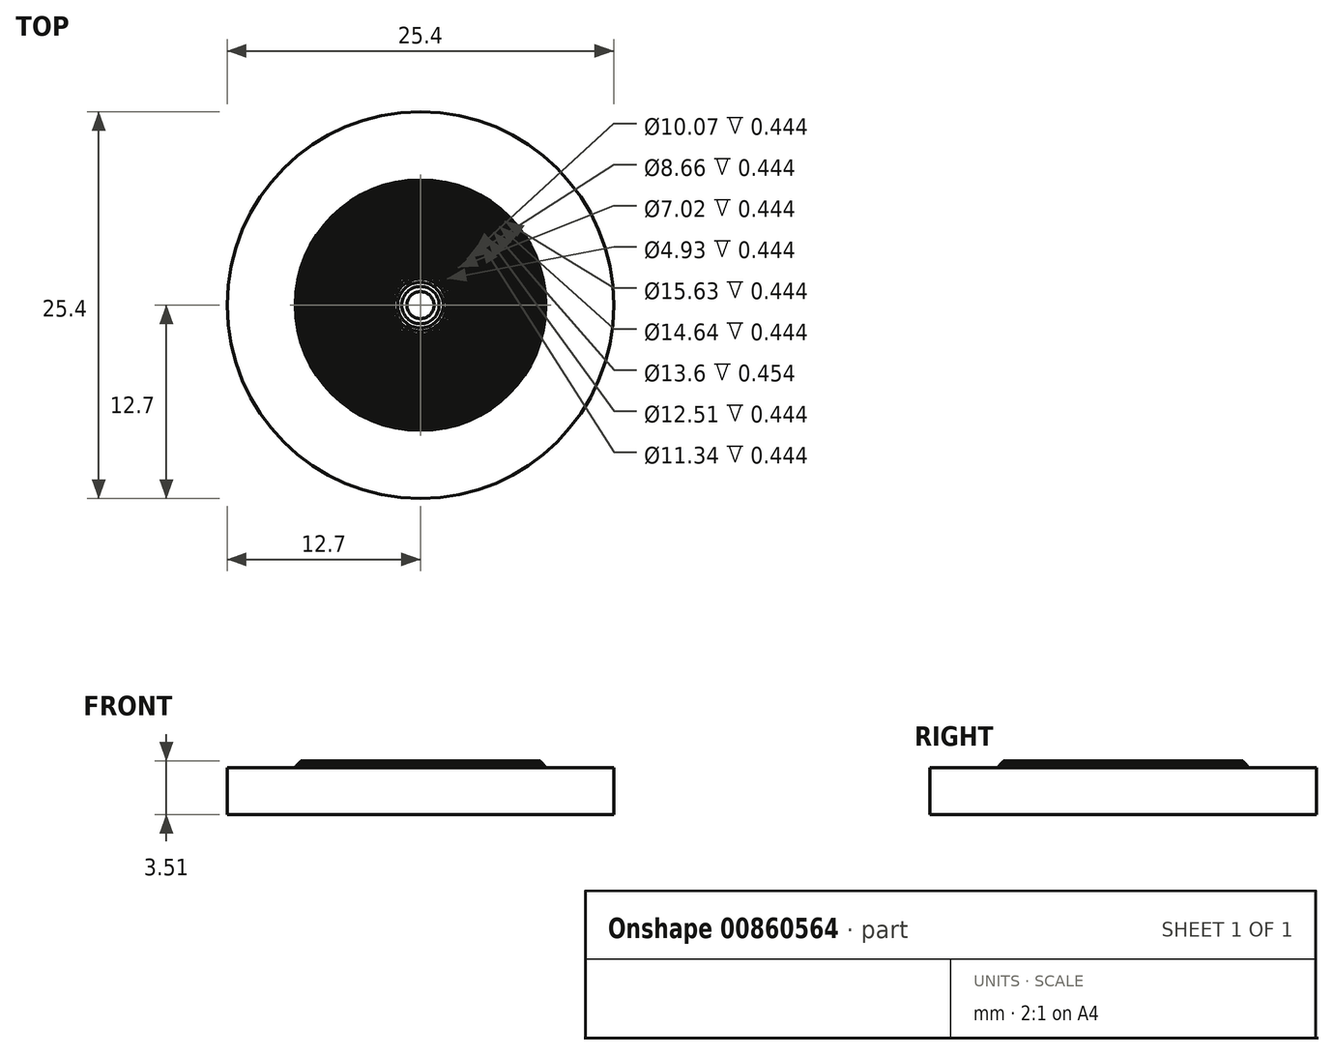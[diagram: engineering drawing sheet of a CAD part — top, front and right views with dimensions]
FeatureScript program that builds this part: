
annotation { "Feature Type Name" : "Feature", "Feature Type Description" : "" }
export const myFeature = defineFeature(function(context is Context, id is Id, definition is map)
    precondition{}
    {
        {
            var Q0;
            Q0=qCreatedBy(makeId("Front.planeOp"),FACE);
            var sketch = newSketch(context, id + "F0", { "sketchPlane" : qUnion([Q0])});
            skLineSegment(sketch, "E0", {"start": v(0, 0) * mm, "end": v(0, 3.5) * mm});
            skLineSegment(sketch, "E1", {"start": v(0, 3.5) * mm, "end": v(0.89, 3.5) * mm});
            skLineSegment(sketch, "E2", {"start": v(0.89, 3.5) * mm, "end": v(0.89, 3.44) * mm});
            skLineSegment(sketch, "E3", {"start": v(1.23, 3.38) * mm, "end": v(1.23, 3.44) * mm});
            skLineSegment(sketch, "E4", {"start": v(1.23, 3.44) * mm, "end": v(0.89, 3.44) * mm});
            skLineSegment(sketch, "E5", {"start": v(1.5, 3.32) * mm, "end": v(1.5, 3.38) * mm});
            skLineSegment(sketch, "E6", {"start": v(1.5, 3.38) * mm, "end": v(1.23, 3.38) * mm});
            skLineSegment(sketch, "E7", {"start": v(1.74, 3.25) * mm, "end": v(1.74, 3.32) * mm});
            skLineSegment(sketch, "E8", {"start": v(1.74, 3.32) * mm, "end": v(1.5, 3.32) * mm});
            skLineSegment(sketch, "E9", {"start": v(1.94, 3.19) * mm, "end": v(1.94, 3.25) * mm});
            skLineSegment(sketch, "E10", {"start": v(1.94, 3.25) * mm, "end": v(1.74, 3.25) * mm});
            skLineSegment(sketch, "E11", {"start": v(2.13, 3.13) * mm, "end": v(2.13, 3.19) * mm});
            skLineSegment(sketch, "E12", {"start": v(2.13, 3.19) * mm, "end": v(1.94, 3.19) * mm});
            skLineSegment(sketch, "E13", {"start": v(2.3, 3.06) * mm, "end": v(2.3, 3.13) * mm});
            skLineSegment(sketch, "E14", {"start": v(2.3, 3.13) * mm, "end": v(2.13, 3.13) * mm});
            skLineSegment(sketch, "E15", {"start": v(2.46, 3.06) * mm, "end": v(2.3, 3.06) * mm});
            skLineSegment(sketch, "E16", {"start": v(2.9, 3.32) * mm, "end": v(2.9, 3.38) * mm});
            skLineSegment(sketch, "E17", {"start": v(2.9, 3.38) * mm, "end": v(2.76, 3.38) * mm});
            skLineSegment(sketch, "E18", {"start": v(3.03, 3.25) * mm, "end": v(3.03, 3.32) * mm});
            skLineSegment(sketch, "E19", {"start": v(3.03, 3.32) * mm, "end": v(2.9, 3.32) * mm});
            skLineSegment(sketch, "E20", {"start": v(3.16, 3.19) * mm, "end": v(3.16, 3.25) * mm});
            skLineSegment(sketch, "E21", {"start": v(3.16, 3.25) * mm, "end": v(3.03, 3.25) * mm});
            skLineSegment(sketch, "E22", {"start": v(2.46, 3.06) * mm, "end": v(2.46, 3.5) * mm});
            skLineSegment(sketch, "E23", {"start": v(2.46, 3.5) * mm, "end": v(2.62, 3.5) * mm});
            skLineSegment(sketch, "E24", {"start": v(2.76, 3.38) * mm, "end": v(2.76, 3.44) * mm});
            skLineSegment(sketch, "E25", {"start": v(2.76, 3.44) * mm, "end": v(2.62, 3.44) * mm});
            skLineSegment(sketch, "E26", {"start": v(3.28, 3.13) * mm, "end": v(3.28, 3.19) * mm});
            skLineSegment(sketch, "E27", {"start": v(3.28, 3.19) * mm, "end": v(3.16, 3.19) * mm});
            skLineSegment(sketch, "E28", {"start": v(3.4, 3.06) * mm, "end": v(3.4, 3.13) * mm});
            skLineSegment(sketch, "E29", {"start": v(3.4, 3.13) * mm, "end": v(3.28, 3.13) * mm});
            skLineSegment(sketch, "E30", {"start": v(3.51, 3.06) * mm, "end": v(3.4, 3.06) * mm});
            skLineSegment(sketch, "E31", {"start": v(3.62, 3.44) * mm, "end": v(3.62, 3.5) * mm});
            skLineSegment(sketch, "E32", {"start": v(3.73, 3.38) * mm, "end": v(3.73, 3.44) * mm});
            skLineSegment(sketch, "E33", {"start": v(3.73, 3.44) * mm, "end": v(3.62, 3.44) * mm});
            skLineSegment(sketch, "E34", {"start": v(3.51, 3.5) * mm, "end": v(3.62, 3.5) * mm});
            skLineSegment(sketch, "E35", {"start": v(3.84, 3.32) * mm, "end": v(3.84, 3.38) * mm});
            skLineSegment(sketch, "E36", {"start": v(3.84, 3.38) * mm, "end": v(3.73, 3.38) * mm});
            skLineSegment(sketch, "E37", {"start": v(3.94, 3.25) * mm, "end": v(3.94, 3.32) * mm});
            skLineSegment(sketch, "E38", {"start": v(3.94, 3.32) * mm, "end": v(3.84, 3.32) * mm});
            skLineSegment(sketch, "E39", {"start": v(4.04, 3.19) * mm, "end": v(4.04, 3.25) * mm});
            skLineSegment(sketch, "E40", {"start": v(4.04, 3.25) * mm, "end": v(3.94, 3.25) * mm});
            skLineSegment(sketch, "E41", {"start": v(4.14, 3.13) * mm, "end": v(4.14, 3.19) * mm});
            skLineSegment(sketch, "E42", {"start": v(4.14, 3.19) * mm, "end": v(4.04, 3.19) * mm});
            skLineSegment(sketch, "E43", {"start": v(4.24, 3.06) * mm, "end": v(4.24, 3.13) * mm});
            skLineSegment(sketch, "E44", {"start": v(4.24, 3.13) * mm, "end": v(4.14, 3.13) * mm});
            skLineSegment(sketch, "E45", {"start": v(4.33, 3.06) * mm, "end": v(4.24, 3.06) * mm});
            skLineSegment(sketch, "E46", {"start": v(4.42, 3.44) * mm, "end": v(4.42, 3.5) * mm});
            skLineSegment(sketch, "E47", {"start": v(4.33, 3.06) * mm, "end": v(4.33, 3.5) * mm});
            skLineSegment(sketch, "E48", {"start": v(4.33, 3.5) * mm, "end": v(4.42, 3.5) * mm});
            skLineSegment(sketch, "E49", {"start": v(4.51, 3.38) * mm, "end": v(4.51, 3.44) * mm});
            skLineSegment(sketch, "E50", {"start": v(4.51, 3.44) * mm, "end": v(4.42, 3.44) * mm});
            skLineSegment(sketch, "E51", {"start": v(4.6, 3.32) * mm, "end": v(4.6, 3.38) * mm});
            skLineSegment(sketch, "E52", {"start": v(4.6, 3.38) * mm, "end": v(4.51, 3.38) * mm});
            skLineSegment(sketch, "E53", {"start": v(4.7, 3.25) * mm, "end": v(4.7, 3.32) * mm});
            skLineSegment(sketch, "E54", {"start": v(4.7, 3.32) * mm, "end": v(4.6, 3.32) * mm});
            skLineSegment(sketch, "E55", {"start": v(4.78, 3.19) * mm, "end": v(4.78, 3.25) * mm});
            skLineSegment(sketch, "E56", {"start": v(4.78, 3.25) * mm, "end": v(4.7, 3.25) * mm});
            skLineSegment(sketch, "E57", {"start": v(4.87, 3.13) * mm, "end": v(4.87, 3.19) * mm});
            skLineSegment(sketch, "E58", {"start": v(4.87, 3.19) * mm, "end": v(4.78, 3.19) * mm});
            skLineSegment(sketch, "E59", {"start": v(4.95, 3.06) * mm, "end": v(4.95, 3.13) * mm});
            skLineSegment(sketch, "E60", {"start": v(4.95, 3.13) * mm, "end": v(4.87, 3.13) * mm});
            skLineSegment(sketch, "E61", {"start": v(5.04, 3.06) * mm, "end": v(4.95, 3.06) * mm});
            skLineSegment(sketch, "E62", {"start": v(5.12, 3.44) * mm, "end": v(5.12, 3.5) * mm});
            skLineSegment(sketch, "E63", {"start": v(5.04, 3.5) * mm, "end": v(5.12, 3.5) * mm});
            skLineSegment(sketch, "E64", {"start": v(5.2, 3.38) * mm, "end": v(5.2, 3.44) * mm});
            skLineSegment(sketch, "E65", {"start": v(5.2, 3.44) * mm, "end": v(5.12, 3.44) * mm});
            skLineSegment(sketch, "E66", {"start": v(5.28, 3.32) * mm, "end": v(5.28, 3.38) * mm});
            skLineSegment(sketch, "E67", {"start": v(5.28, 3.38) * mm, "end": v(5.2, 3.38) * mm});
            skLineSegment(sketch, "E68", {"start": v(5.36, 3.25) * mm, "end": v(5.36, 3.32) * mm});
            skLineSegment(sketch, "E69", {"start": v(5.36, 3.32) * mm, "end": v(5.28, 3.32) * mm});
            skLineSegment(sketch, "E70", {"start": v(5.44, 3.19) * mm, "end": v(5.44, 3.25) * mm});
            skLineSegment(sketch, "E71", {"start": v(5.44, 3.25) * mm, "end": v(5.36, 3.25) * mm});
            skLineSegment(sketch, "E72", {"start": v(5.52, 3.13) * mm, "end": v(5.52, 3.19) * mm});
            skLineSegment(sketch, "E73", {"start": v(5.52, 3.19) * mm, "end": v(5.44, 3.19) * mm});
            skLineSegment(sketch, "E74", {"start": v(5.6, 3.06) * mm, "end": v(5.6, 3.13) * mm});
            skLineSegment(sketch, "E75", {"start": v(5.6, 3.13) * mm, "end": v(5.52, 3.13) * mm});
            skLineSegment(sketch, "E76", {"start": v(5.67, 3.06) * mm, "end": v(5.6, 3.06) * mm});
            skLineSegment(sketch, "E77", {"start": v(5.74, 3.44) * mm, "end": v(5.74, 3.5) * mm});
            skLineSegment(sketch, "E78", {"start": v(5.67, 3.5) * mm, "end": v(5.74, 3.5) * mm});
            skLineSegment(sketch, "E79", {"start": v(5.82, 3.38) * mm, "end": v(5.82, 3.44) * mm});
            skLineSegment(sketch, "E80", {"start": v(5.82, 3.44) * mm, "end": v(5.74, 3.44) * mm});
            skLineSegment(sketch, "E81", {"start": v(5.9, 3.32) * mm, "end": v(5.9, 3.38) * mm});
            skLineSegment(sketch, "E82", {"start": v(5.9, 3.38) * mm, "end": v(5.82, 3.38) * mm});
            skLineSegment(sketch, "E83", {"start": v(5.97, 3.25) * mm, "end": v(5.97, 3.32) * mm});
            skLineSegment(sketch, "E84", {"start": v(5.97, 3.32) * mm, "end": v(5.9, 3.32) * mm});
            skLineSegment(sketch, "E85", {"start": v(6.04, 3.19) * mm, "end": v(6.04, 3.25) * mm});
            skLineSegment(sketch, "E86", {"start": v(6.04, 3.25) * mm, "end": v(5.97, 3.25) * mm});
            skLineSegment(sketch, "E87", {"start": v(6.18, 3.06) * mm, "end": v(6.18, 3.13) * mm});
            skLineSegment(sketch, "E88", {"start": v(6.11, 3.13) * mm, "end": v(6.11, 3.19) * mm});
            skLineSegment(sketch, "E89", {"start": v(6.11, 3.19) * mm, "end": v(6.04, 3.19) * mm});
            skLineSegment(sketch, "E90", {"start": v(6.18, 3.13) * mm, "end": v(6.11, 3.13) * mm});
            skLineSegment(sketch, "E91", {"start": v(6.25, 3.06) * mm, "end": v(6.18, 3.06) * mm});
            skLineSegment(sketch, "E92", {"start": v(6.32, 3.44) * mm, "end": v(6.32, 3.5) * mm});
            skLineSegment(sketch, "E93", {"start": v(6.25, 3.06) * mm, "end": v(6.25, 3.5) * mm});
            skLineSegment(sketch, "E94", {"start": v(6.25, 3.5) * mm, "end": v(6.32, 3.5) * mm});
            skLineSegment(sketch, "E95", {"start": v(6.4, 3.38) * mm, "end": v(6.4, 3.44) * mm});
            skLineSegment(sketch, "E96", {"start": v(6.4, 3.44) * mm, "end": v(6.32, 3.44) * mm});
            skLineSegment(sketch, "E97", {"start": v(6.46, 3.32) * mm, "end": v(6.46, 3.38) * mm});
            skLineSegment(sketch, "E98", {"start": v(6.46, 3.38) * mm, "end": v(6.4, 3.38) * mm});
            skLineSegment(sketch, "E99", {"start": v(6.53, 3.25) * mm, "end": v(6.53, 3.32) * mm});
            skLineSegment(sketch, "E100", {"start": v(6.53, 3.32) * mm, "end": v(6.46, 3.32) * mm});
            skLineSegment(sketch, "E101", {"start": v(6.6, 3.19) * mm, "end": v(6.6, 3.25) * mm});
            skLineSegment(sketch, "E102", {"start": v(6.6, 3.25) * mm, "end": v(6.53, 3.25) * mm});
            skLineSegment(sketch, "E103", {"start": v(6.67, 3.13) * mm, "end": v(6.67, 3.19) * mm});
            skLineSegment(sketch, "E104", {"start": v(6.67, 3.19) * mm, "end": v(6.6, 3.19) * mm});
            skLineSegment(sketch, "E105", {"start": v(6.73, 3.05) * mm, "end": v(6.73, 3.13) * mm});
            skLineSegment(sketch, "E106", {"start": v(6.73, 3.13) * mm, "end": v(6.67, 3.13) * mm});
            skLineSegment(sketch, "E107", {"start": v(6.8, 3.05) * mm, "end": v(6.73, 3.05) * mm});
            skLineSegment(sketch, "E108", {"start": v(6.87, 3.44) * mm, "end": v(6.87, 3.5) * mm});
            skLineSegment(sketch, "E109", {"start": v(6.8, 3.5) * mm, "end": v(6.87, 3.5) * mm});
            skLineSegment(sketch, "E110", {"start": v(6.93, 3.38) * mm, "end": v(6.93, 3.44) * mm});
            skLineSegment(sketch, "E111", {"start": v(6.93, 3.44) * mm, "end": v(6.87, 3.44) * mm});
            skLineSegment(sketch, "E112", {"start": v(7, 3.32) * mm, "end": v(7, 3.38) * mm});
            skLineSegment(sketch, "E113", {"start": v(7, 3.38) * mm, "end": v(6.93, 3.38) * mm});
            skLineSegment(sketch, "E114", {"start": v(7.06, 3.25) * mm, "end": v(7.06, 3.32) * mm});
            skLineSegment(sketch, "E115", {"start": v(7.06, 3.32) * mm, "end": v(7, 3.32) * mm});
            skLineSegment(sketch, "E116", {"start": v(7.2, 3.13) * mm, "end": v(7.2, 3.19) * mm});
            skLineSegment(sketch, "E117", {"start": v(7.13, 3.19) * mm, "end": v(7.13, 3.25) * mm});
            skLineSegment(sketch, "E118", {"start": v(7.26, 3.06) * mm, "end": v(7.26, 3.13) * mm});
            skLineSegment(sketch, "E119", {"start": v(7.38, 3.44) * mm, "end": v(7.38, 3.5) * mm});
            skLineSegment(sketch, "E120", {"start": v(7.13, 3.25) * mm, "end": v(7.06, 3.25) * mm});
            skLineSegment(sketch, "E121", {"start": v(7.2, 3.19) * mm, "end": v(7.13, 3.19) * mm});
            skLineSegment(sketch, "E122", {"start": v(7.26, 3.13) * mm, "end": v(7.2, 3.13) * mm});
            skLineSegment(sketch, "E123", {"start": v(7.32, 3.06) * mm, "end": v(7.26, 3.06) * mm});
            skLineSegment(sketch, "E124", {"start": v(7.32, 3.5) * mm, "end": v(7.38, 3.5) * mm});
            skLineSegment(sketch, "E125", {"start": v(7.44, 3.38) * mm, "end": v(7.44, 3.44) * mm});
            skLineSegment(sketch, "E126", {"start": v(7.5, 3.32) * mm, "end": v(7.5, 3.38) * mm});
            skLineSegment(sketch, "E127", {"start": v(7.57, 3.25) * mm, "end": v(7.57, 3.32) * mm});
            skLineSegment(sketch, "E128", {"start": v(7.63, 3.19) * mm, "end": v(7.63, 3.25) * mm});
            skLineSegment(sketch, "E129", {"start": v(7.7, 3.13) * mm, "end": v(7.7, 3.19) * mm});
            skLineSegment(sketch, "E130", {"start": v(7.75, 3.06) * mm, "end": v(7.75, 3.13) * mm});
            skLineSegment(sketch, "E131", {"start": v(7.44, 3.44) * mm, "end": v(7.38, 3.44) * mm});
            skLineSegment(sketch, "E132", {"start": v(7.5, 3.38) * mm, "end": v(7.44, 3.38) * mm});
            skLineSegment(sketch, "E133", {"start": v(7.57, 3.32) * mm, "end": v(7.5, 3.32) * mm});
            skLineSegment(sketch, "E134", {"start": v(7.63, 3.25) * mm, "end": v(7.57, 3.25) * mm});
            skLineSegment(sketch, "E135", {"start": v(7.7, 3.19) * mm, "end": v(7.63, 3.19) * mm});
            skLineSegment(sketch, "E136", {"start": v(7.75, 3.13) * mm, "end": v(7.7, 3.13) * mm});
            skLineSegment(sketch, "E137", {"start": v(7.81, 3.06) * mm, "end": v(7.75, 3.06) * mm});
            skLineSegment(sketch, "E138", {"start": v(7.88, 3.44) * mm, "end": v(7.88, 3.5) * mm});
            skLineSegment(sketch, "E139", {"start": v(7.81, 3.5) * mm, "end": v(7.88, 3.5) * mm});
            skLineSegment(sketch, "E140", {"start": v(7.94, 3.38) * mm, "end": v(7.94, 3.44) * mm});
            skLineSegment(sketch, "E141", {"start": v(8, 3.32) * mm, "end": v(8, 3.38) * mm});
            skLineSegment(sketch, "E142", {"start": v(8.06, 3.25) * mm, "end": v(8.06, 3.32) * mm});
            skLineSegment(sketch, "E143", {"start": v(8.11, 3.19) * mm, "end": v(8.11, 3.25) * mm});
            skLineSegment(sketch, "E144", {"start": v(8.17, 3.13) * mm, "end": v(8.17, 3.19) * mm});
            skLineSegment(sketch, "E145", {"start": v(8.23, 3.06) * mm, "end": v(8.23, 3.13) * mm});
            skLineSegment(sketch, "E146", {"start": v(7.94, 3.44) * mm, "end": v(7.88, 3.44) * mm});
            skLineSegment(sketch, "E147", {"start": v(8, 3.38) * mm, "end": v(7.93, 3.38) * mm});
            skLineSegment(sketch, "E148", {"start": v(8.06, 3.32) * mm, "end": v(8, 3.32) * mm});
            skLineSegment(sketch, "E149", {"start": v(8.11, 3.25) * mm, "end": v(8.06, 3.25) * mm});
            skLineSegment(sketch, "E150", {"start": v(8.17, 3.19) * mm, "end": v(8.11, 3.19) * mm});
            skLineSegment(sketch, "E151", {"start": v(8.23, 3.13) * mm, "end": v(8.17, 3.13) * mm});
            skLineSegment(sketch, "E152", {"start": v(8.3, 3.06) * mm, "end": v(8.23, 3.06) * mm});
            skLineSegment(sketch, "E153", {"start": v(12.7, 0) * mm, "end": v(12.7, 3.06) * mm});
            skLineSegment(sketch, "E154", {"start": v(12.7, 3.06) * mm, "end": v(8.3, 3.06) * mm});
            skLineSegment(sketch, "E155", {"start": v(2.62, 3.5) * mm, "end": v(2.62, 3.44) * mm});
            skLineSegment(sketch, "E156", {"start": v(3.51, 3.5) * mm, "end": v(3.51, 3.06) * mm});
            skLineSegment(sketch, "E157", {"start": v(5.04, 3.06) * mm, "end": v(5.04, 3.5) * mm});
            skLineSegment(sketch, "E158", {"start": v(5.67, 3.06) * mm, "end": v(5.67, 3.5) * mm});
            skLineSegment(sketch, "E159", {"start": v(6.8, 3.05) * mm, "end": v(6.8, 3.5) * mm});
            skLineSegment(sketch, "E160", {"start": v(7.32, 3.06) * mm, "end": v(7.32, 3.5) * mm});
            skLineSegment(sketch, "E161", {"start": v(7.81, 3.06) * mm, "end": v(7.81, 3.5) * mm});
            skLineSegment(sketch, "E162", {"start": v(0, 0) * mm, "end": v(12.7, 0) * mm});
            skSolve(sketch);
        }
        {
            var Q0;
            Q0=makeQuery(id+"F0.imprint","IMPRINT",FACE,{"disambiguationData":[TD([[makeQuery(id+"F0.imprint","IMPRINT",EDGE,{"derivedFrom":sQuery(id+"F0.wireOp",EDGE,"E0")}),-1.0]])]});
            var Q1;
            Q1=sQuery(id+"F0.wireOp",EDGE,"E0");
            revolve(context, id + "F1", {"surfaceOperationType" : NewSurfaceOperationType.NEW, "entities" : qUnion([Q0]), "axis" : qUnion([Q1]), "revolveType" : RevolveType.FULL});
        }
    });
